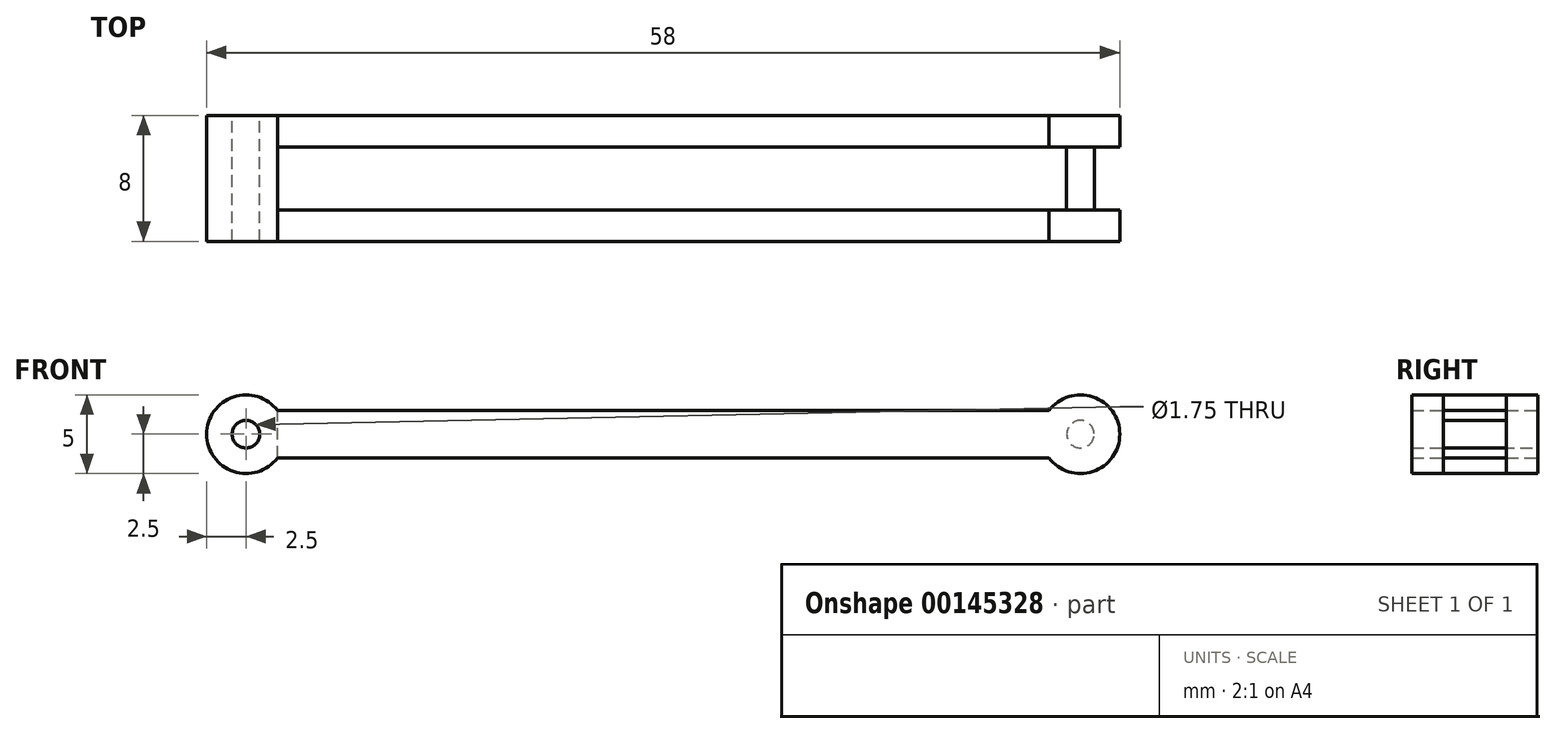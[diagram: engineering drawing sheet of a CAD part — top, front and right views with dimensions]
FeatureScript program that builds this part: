
annotation { "Feature Type Name" : "Feature", "Feature Type Description" : "" }
export const myFeature = defineFeature(function(context is Context, id is Id, definition is map)
    precondition{}
    {
        {
            var Q0;
            Q0=qCreatedBy(makeId("Front.planeOp"),FACE);
            var sketch = newSketch(context, id + "F0", { "sketchPlane" : qUnion([Q0])});
            skCircle(sketch, "E0", {"center": v(-25, 0) * mm, "radius": 0.87 * mm});
            skCircle(sketch, "E1", {"center": v(28, 0) * mm, "radius": 0.87 * mm});
            skLineSegment(sketch, "E2.bottom", {"start": v(-23, -1.5) * mm, "end": v(26, -1.5) * mm});
            skLineSegment(sketch, "E2.top", {"start": v(-23, 1.5) * mm, "end": v(26, 1.5) * mm});
            skArc(sketch, "E3", {"start": v(-23, 1.5) * mm, "mid": v(-27.5, 0) * mm, "end": v(-23, -1.5) * mm});
            skArc(sketch, "E4", {"start": v(26, -1.5) * mm, "mid": v(30.5, 0) * mm, "end": v(26, 1.5) * mm});
            skSolve(sketch);
        }
        {
            var Q0;
            Q0=makeQuery(id+"F0.imprint","IMPRINT",FACE,{"disambiguationData":[TD([[makeQuery(id+"F0.imprint","IMPRINT",EDGE,{"derivedFrom":sQuery(id+"F0.wireOp",EDGE,"E0")}),-1.0]])]});
            extrude(context, id + "F1", {"entities" : qUnion([Q0]), "endBound" : BoundingType.SYMMETRIC, "depth" : 8 * mm});
        }
        {
            var Q0;
            Q0=qCreatedBy(makeId("Front.planeOp"),FACE);
            var sketch = newSketch(context, id + "F2", { "sketchPlane" : qUnion([Q0])});
            skCircle(sketch, "E5", {"center": v(28, 0) * mm, "radius": 2.5 * mm});
            skArc(sketch, "E6.0", {"start": v(26, -1.5) * mm, "mid": v(30.5, 0) * mm, "end": v(26, 1.5) * mm});
            skSolve(sketch);
        }
        {
            var Q0;
            Q0 = qSketchRegion(id + "F2", true);
            extrude(context, id + "F3", {"entities" : qUnion([Q0]), "operationType" : NewBodyOperationType.REMOVE, "endBound" : BoundingType.SYMMETRIC, "oppositeDirection" : true, "depth" : 4 * mm});
        }
        {
            var Q0;
            Q0=makeQuery(id+"F0.imprint","IMPRINT",FACE,{"disambiguationData":[TD([[makeQuery(id+"F0.imprint","IMPRINT",EDGE,{"derivedFrom":sQuery(id+"F0.wireOp",EDGE,"E1")}),1.0]])]});
            extrude(context, id + "F4", {"entities" : qUnion([Q0]), "operationType" : NewBodyOperationType.ADD, "endBound" : BoundingType.SYMMETRIC, "depth" : 8 * mm});
        }
        {
            var Q0;
            Q0=qCreatedBy(makeId("Top.planeOp"),FACE);
            var sketch = newSketch(context, id + "F5", { "sketchPlane" : qUnion([Q0])});
            skLineSegment(sketch, "E7.bottom", {"start": v(26, -2) * mm, "end": v(-23, -2) * mm});
            skLineSegment(sketch, "E7.top", {"start": v(26, 2) * mm, "end": v(-23, 2) * mm});
            skLineSegment(sketch, "E7.left", {"start": v(26, -2) * mm, "end": v(26, 2) * mm});
            skLineSegment(sketch, "E7.right", {"start": v(-23, -2) * mm, "end": v(-23, 2) * mm});
            skSolve(sketch);
        }
        {
            var Q0;
            Q0 = qSketchRegion(id + "F5", true);
            extrude(context, id + "F6", {"entities" : qUnion([Q0]), "operationType" : NewBodyOperationType.REMOVE, "endBound" : BoundingType.SYMMETRIC, "oppositeDirection" : true, "depth" : 5 * mm});
        }
    });
